# Revit family: SP4250 W_REVIT
name_source: partatom
category: Mechanical Equipment
revit_build: Autodesk Revit 2014 (Build: 20130215_1615(x64)
units: mm (PartAtom-declared; Revit-internal decimal feet)

## types (1)
- Standard
    Connector_10_Diameter = 0' - 0"
    Connector_11_Diameter = 0' - 0"
    Connector_1_Diameter = 0' - 0"
    Connector_2_Diameter = 0' - 0"
    Connector_3_Diameter = 0' - 0"
    Connector_4_Diameter = 0' - 0"
    Connector_5_Diameter = 0' - 0"
    Connector_6_Diameter = 0' - 0"
    Connector_7_Diameter = 0' - 0"
    Connector_8_Diameter = 0' - 0"
    Connector_9_Diameter = 0' - 0"
    Description = Electric Resistive Humidifier Weather proof
    Design Status = 1
    Manufacturer = Neptronic
    Model = SK370-W, SK380-W, SK390-W
    Part Number = SP4250 W_REVIT
    URL = www.neptronic.com
    d191 = 0' - 1 1/32"
    d193 = 0' - 0 1/4"
    d195 = 0' - 1 9/32"
    d197 = 0' - 1 9/32"
    d199 = 0' - 0 1/4"
    d201 = 0' - 0 1/4"
    d203 = 0' - 0 1/4"
    d205 = 0' - 0 1/4"
    d207 = 0' - 0 1/4"
    d209 = 0' - 0 1/4"
    d211 = 0' - 0 1/4"
    d213 = 0' - 0 1/4"
    d215 = 0' - 0 1/4"
    d217 = 0' - 0 1/4"
    d219 = 0' - 0 1/4"
    d221 = 0' - 1 9/32"
    d223 = 0' - 0 1/4"
    d225 = 0' - 0 1/4"
    d227 = 0' - 0 1/4"
    d229 = 2' - 2 1/16"
    d231 = 0' - 0 1/8"
    d240 = 0' - 0"

## geometry (parser evidence)
native form markers: Sweep x1
no freeform markers — native parametric forms only
